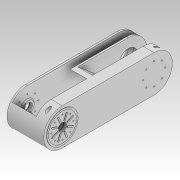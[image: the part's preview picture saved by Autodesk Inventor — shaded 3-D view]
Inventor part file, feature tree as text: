
AUTODESK INVENTOR PART (.ipt)
format: ipt  version: 2020 (Build 240168000, 168)  size: 656,896 bytes
history: native  units: mm
features: sketch x30, extrude x28, projected_geometry x6, plane x5, pattern_circular x2, fillet x2, revolve x2, chamfer x1, loft x1, other x1
ambient origin geometry x8: Origin, YZ Plane, XZ Plane, XY Plane, X Axis, Y Axis, Z Axis, Center Point
bodies: Solid1 (feature_tree)
feature tree (78):
  extrude  "Extrusion1"  Depth=250.0mm
  extrude  "Extrusion2"  Depth=100.0mm TaperAngle=0.0deg
  extrude  "Extrusion3"  TaperAngle=0.0deg  [1 undecoded]
  extrude  "Extrusion4"  Depth=10.0mm
  extrude  "Extrusion5"  Depth=1.0mm
  pattern_circular  "Circular Pattern1"  Count=8 Angle=360.0deg
  plane  "Work Plane1"
  plane  "Work Plane2"
  extrude  "Extrusion6"  Depth=30.0mm
  extrude  "Extrusion7"  Depth=10.0mm
  extrude  "Extrusion8"  Depth=10.0mm
  extrude  "Extrusion9"  [1 undecoded]
  chamfer  "Chamfer1"  Distance=10.0mm
  extrude  "Extrusion13"  Depth=10.0mm TaperAngle=0.0deg
  extrude  "Extrusion14"  Depth=3.0mm TaperAngle=0.0deg
  extrude  "Extrusion15"  Depth=3.0mm
  extrude  "Extrusion16"  Depth=3.0mm
  extrude  "Extrusion17"  Depth=80.0mm
  extrude  "Extrusion18"  Depth=60.0mm
  extrude  "Extrusion19"  Depth=80.0mm TaperAngle=360.0deg
  extrude  "Extrusion20"  Depth=15.5mm TaperAngle=0.0deg
  fillet  "Fillet2"  Radius=22.1mm
  pattern_circular  "Circular Pattern2"  Count=8 Angle=360.0deg
  extrude  "Extrusion21"  Depth=10.0mm
  extrude  "Extrusion22"  Depth=6.0mm
  plane  "Work Plane3"
  revolve  "Revolution1"  [1 undecoded]
  revolve  "Revolution2"  [1 undecoded]
  plane  "Work Plane4"
  extrude  "Extrusion23"  Depth=25.0mm
  extrude  "Extrusion24"  Depth=6.0mm
  fillet  "Fillet3"  Radius=96.8mm
  loft  "Loft1"
  extrude  "Extrusion25"  Depth=6.0mm
  extrude  "Extrusion26"  Depth=6.0mm
  extrude  "Extrusion27"  Depth=1.0mm
  extrude  "Extrusion28"  Depth=5.0mm
  plane  "Work Plane5"
  extrude  "Extrusion29"  Depth=6.0mm
  extrude  "Extrusion30"  TaperAngle=90.0deg  [1 undecoded]
  extrude  "Extrusion32"  Depth=6.0mm
  sketch  "Sketch1"  dims[d0=50.0mm d1=250.0mm]
  sketch  "Sketch2"  dims[d2=50.0mm d3=100.0mm d4=0.0mm]
  sketch  "Sketch4"  dims[d5=5.0mm d7=0.0mm d8=0.0mm]
  sketch  "Sketch5"  dims[d11=10.0mm d12=0.0mm d14=85.0mm]
  sketch  "Sketch7"  dims[d15=1.0mm d16=0.0mm d17=30.0mm]
  projected_geometry  "Projected Loop1"
  sketch  "Sketch8"  dims[d18=3.3mm]
  projected_geometry  "Projected Loop2"
  projected_geometry  "Projected Loop4"
  sketch  "Sketch9"  dims[d19=15.0mm d20=0.0mm d21=80.0mm d22=360.0deg]
  sketch  "Sketch10"  dims[d24=30.0mm d25=30.0mm]
  sketch  "Sketch14"  dims[d30=-5.0mm d31=10.0mm]
  sketch  "Sketch15"  dims[d32=10.0mm d33=10.0mm]
  sketch  "Sketch16"  dims[d34=31.5mm d35=0.0mm d36=-5.0mm d38=10.0mm d39=0.0mm]
  sketch  "Sketch17"  dims[d40=22.1mm d41=10.0mm d42=0.0mm]
  sketch  "Sketch18"  dims[d43=5.0mm d44=3.0mm d45=0.0mm]
  sketch  "Sketch19"  dims[d56=3.0mm d57=2.0mm d58=45.0deg d62=95.1mm]
  sketch  "Sketch20"  dims[d63=10.0mm d64=0.0mm d65=3.0mm]
  sketch  "Sketch21"  dims[d66=0.5mm d67=0.0mm d68=80.0mm]
  sketch  "Sketch22"  dims[d69=15.5mm d70=0.0mm d71=60.0mm]
  sketch  "Sketch23"  dims[d72=3.2mm d73=80.0mm d75=360.0deg]
  other  "Work Axis1"
  sketch  "Sketch24"  dims[d77=15.5mm d78=0.0mm d79=15.5mm d80=0.0mm d81=22.1mm]
  projected_geometry  "Projected Loop5"
  projected_geometry  "Projected Loop6"
  sketch  "Sketch26"  dims[d82=0.0mm d83=0.0mm]
  sketch  "Sketch27"  dims[d84=76.0mm]
  sketch  "Sketch28"  dims[d85=0.1mm d86=0.0mm]
  sketch  "Sketch29"  dims[d87=15.0mm]
  sketch  "Sketch30"  dims[d88=2.0mm]
  sketch  "Sketch31"  dims[d89=22.5mm]
  sketch  "Sketch32"  dims[d90=0.8mm d91=0.0mm]
  sketch  "Sketch33"  dims[d92=0.2mm d93=80.0mm d94=360.0deg]
  projected_geometry  "Projected Loop7"
  sketch  "Sketch34"  dims[d96=24.43461mm d97=10.0mm]
  sketch  "Sketch35"  dims[d98=8.0mm d99=6.0mm]
  sketch  "Sketch38"  dims[d100=8.0mm d101=6.0mm d102=23.749mm d103=0.0mm d104=25.0mm d105=16.1mm d106=96.8mm d107=0.0mm d108=0.0mm d109=2.5mm d110=5.2mm d111=1.0mm d112=5.0mm d113=5.2mm d114=90.0deg d115=15.0mm d116=25.0mm d117=25.0mm d118=19.0mm d119=19.0mm d120=2.7mm d122=4.0mm d123=0.0mm d124=5.5mm d125=2.0mm d126=0.0mm d127=90.0deg d128=2.0mm d129=18.8mm d130=0.0mm d131=111.25mm d132=0.0mm d133=6.0mm d134=4.0mm d135=0.0mm d136=1.0mm d137=1.0mm d138=0.0mm d139=-7.0mm d140=1.0mm d141=1.0mm d142=0.0mm d143=7.0mm d144=5.0mm d145=6.0mm d146=0.0mm d147=90.0deg d148=0.0mm d149=90.0deg d150=3.0mm d151=10.0mm d152=0.0mm d155=110.0mm d156=0.0mm d157=0.0mm d159=30.0deg d160=6.0mm]
note: 5 required parameter values undecoded (feature->parameter linkage not recoverable at this tier; creation-order binding heuristic only, values carry confidence <= 0.55)